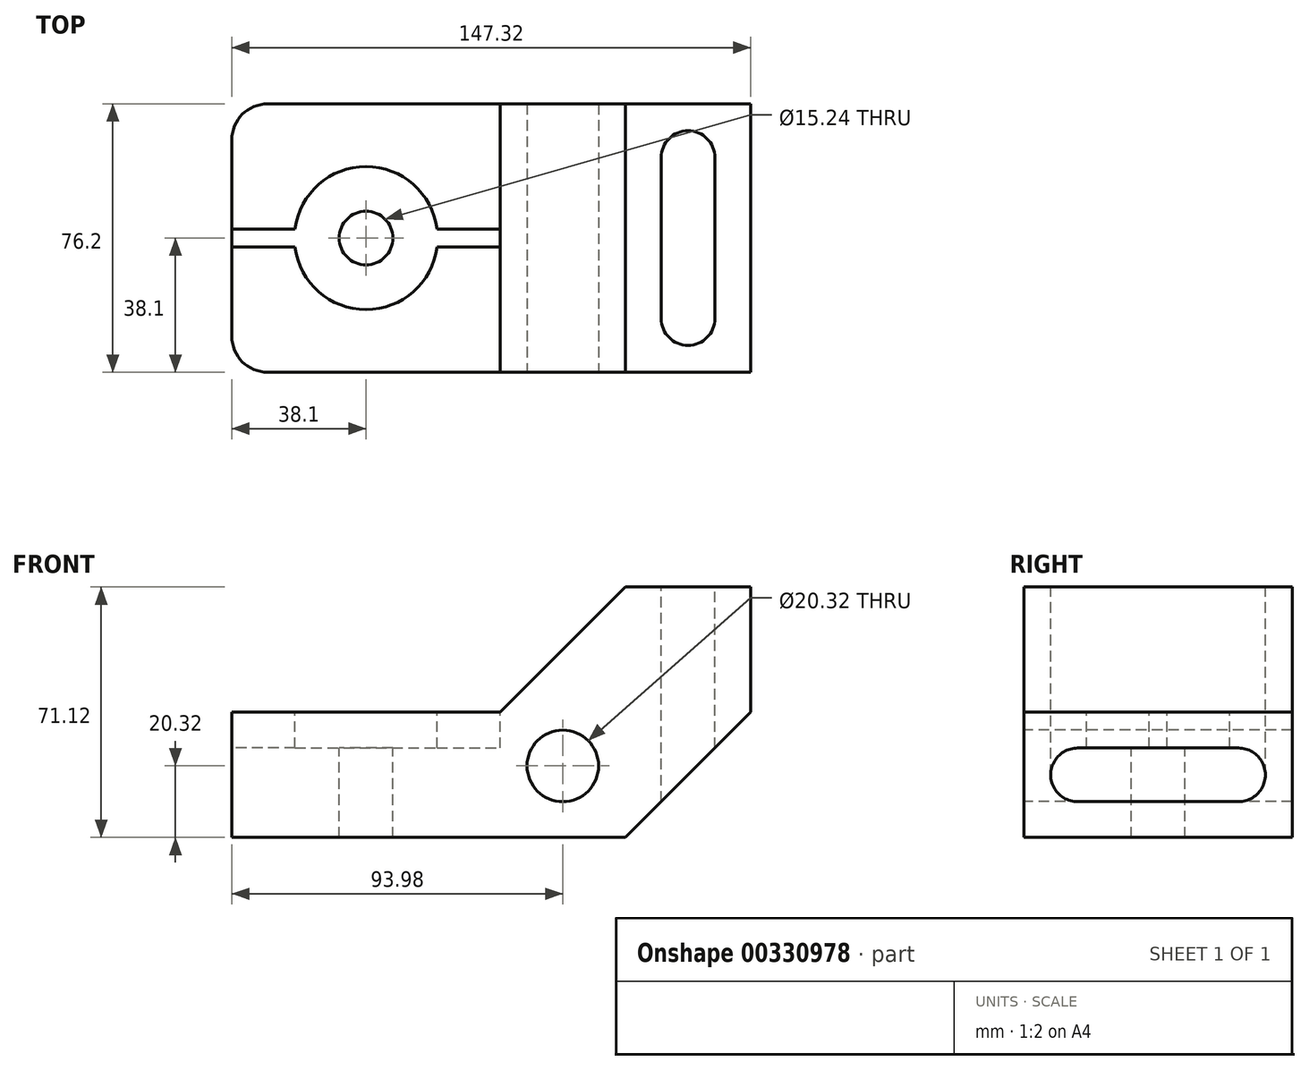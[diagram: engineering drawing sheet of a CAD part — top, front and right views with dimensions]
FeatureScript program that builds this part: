
annotation { "Feature Type Name" : "Feature", "Feature Type Description" : "" }
export const myFeature = defineFeature(function(context is Context, id is Id, definition is map)
    precondition{}
    {
        {
            var Q0;
            Q0=qCreatedBy(makeId("Front.planeOp"),FACE);
            var sketch = newSketch(context, id + "F0", { "sketchPlane" : qUnion([Q0])});
            skLineSegment(sketch, "E0.bottom", {"start": v(0, 0) * mm, "end": v(111.76, 0) * mm});
            skLineSegment(sketch, "E0.top", {"start": v(111.76, 71.12) * mm, "end": v(147.32, 71.12) * mm});
            skLineSegment(sketch, "E0.left", {"start": v(0, 0) * mm, "end": v(0, 35.56) * mm});
            skLineSegment(sketch, "E0.right", {"start": v(147.32, 35.56) * mm, "end": v(147.32, 71.12) * mm});
            skLineSegment(sketch, "E1", {"start": v(0, 35.56) * mm, "end": v(76.2, 35.56) * mm});
            skLineSegment(sketch, "E2", {"start": v(76.2, 35.56) * mm, "end": v(111.76, 71.12) * mm});
            skLineSegment(sketch, "E3", {"start": v(147.32, 71.12) * mm, "end": v(147.32, 35.56) * mm});
            skLineSegment(sketch, "E4", {"start": v(147.32, 35.56) * mm, "end": v(111.76, 0) * mm});
            skLineSegment(sketch, "E5", {"start": v(111.76, 0) * mm, "end": v(0, 0) * mm});
            skPoint(sketch, "E6.orphan", {"position": v(0, 71.12) * mm});
            skPoint(sketch, "E7.orphan", {"position": v(147.32, 0) * mm});
            skSolve(sketch);
        }
        {
            var Q0;
            Q0 = qSketchRegion(id + "F0", true);
            extrude(context, id + "F1", {"entities" : qUnion([Q0]), "depth" : 76.2 * mm});
        }
        {
            var Q0;
            Q0=makeQuery(id+"F1.opExtrude","CAP_FACE",FACE,{"disambiguationData":[OSD([sQuery(id+"F0.wireOp",EDGE,"E0.left"),sQuery(id+"F0.wireOp",EDGE,"E1"),sQuery(id+"F0.wireOp",EDGE,"E2"),sQuery(id+"F0.wireOp",EDGE,"E0.top"),sQuery(id+"F0.wireOp",EDGE,"E3"),sQuery(id+"F0.wireOp",EDGE,"E4"),sQuery(id+"F0.wireOp",EDGE,"E5")])],"isStart":false});
            var sketch = newSketch(context, id + "F2", { "sketchPlane" : qUnion([Q0])});
            skCircle(sketch, "E8", {"center": v(93.98, 20.32) * mm, "radius": 10.16 * mm});
            skSolve(sketch);
        }
        {
            var Q0;
            Q0 = qSketchRegion(id + "F2", true);
            extrude(context, id + "F3", {"entities" : qUnion([Q0]), "operationType" : NewBodyOperationType.REMOVE, "endBound" : BoundingType.THROUGH_ALL, "oppositeDirection" : true, "depth" : 25.4 * mm});
        }
        {
            var Q0;
            Q0=makeQuery(id+"F1.opExtrude","SWEPT_FACE",FACE,{"disambiguationData":[OSD([sQuery(id+"F0.wireOp",EDGE,"E1")])]});
            var sketch = newSketch(context, id + "F4", { "sketchPlane" : qUnion([Q0])});
            skCircle(sketch, "E9", {"center": v(38.1, -38.1) * mm, "radius": 7.62 * mm});
            skPoint(sketch, "E9.centerSnap0", {"position": v(0, -38.1) * mm});
            skPoint(sketch, "E9.centerSnap1", {"position": v(38.1, 0) * mm});
            skSolve(sketch);
        }
        {
            var Q0;
            Q0 = qSketchRegion(id + "F4", true);
            extrude(context, id + "F5", {"entities" : qUnion([Q0]), "operationType" : NewBodyOperationType.REMOVE, "endBound" : BoundingType.THROUGH_ALL, "oppositeDirection" : true, "depth" : 25.4 * mm});
        }
        {
            var Q0;
            Q0=makeQuery(id+"F1.opExtrude","SWEPT_FACE",FACE,{"disambiguationData":[OSD([sQuery(id+"F0.wireOp",EDGE,"E1")])]});
            var sketch = newSketch(context, id + "F6", { "sketchPlane" : qUnion([Q0])});
            skArc(sketch, "E10", {"start": v(17.94, -40.64) * mm, "mid": v(38.1, -58.42) * mm, "end": v(58.26, -40.64) * mm});
            skLineSegment(sketch, "E11", {"start": v(58.26, -35.56) * mm, "end": v(76.2, -35.56) * mm});
            skLineSegment(sketch, "E12", {"start": v(58.26, -40.64) * mm, "end": v(76.2, -40.64) * mm});
            skLineSegment(sketch, "E13", {"start": v(17.94, -40.64) * mm, "end": v(0, -40.64) * mm});
            skLineSegment(sketch, "E14", {"start": v(17.94, -35.56) * mm, "end": v(0, -35.56) * mm});
            skLineSegment(sketch, "E15", {"start": v(38.1, -38.1) * mm, "end": v(-36.03, -38.1) * mm, "construction": true});
            skLineSegment(sketch, "E16", {"start": v(76.2, -35.56) * mm, "end": v(76.2, -40.64) * mm});
            skLineSegment(sketch, "E17", {"start": v(0, -40.64) * mm, "end": v(0, -35.56) * mm});
            skArc(sketch, "E18.trimOffspring", {"start": v(58.26, -35.56) * mm, "mid": v(38.1, -17.78) * mm, "end": v(17.94, -35.56) * mm});
            skSolve(sketch);
        }
        {
            var Q0;
            Q0 = qSketchRegion(id + "F6", true);
            extrude(context, id + "F7", {"entities" : qUnion([Q0]), "operationType" : NewBodyOperationType.REMOVE, "oppositeDirection" : true, "depth" : 10.16 * mm});
        }
        {
            var Q0;
            Q0=makeQuery(id+"F1.opExtrude","SWEPT_FACE",FACE,{"disambiguationData":[OSD([sQuery(id+"F0.wireOp",EDGE,"E0.top")])]});
            var sketch = newSketch(context, id + "F8", { "sketchPlane" : qUnion([Q0])});
            skLineSegment(sketch, "E19", {"start": v(121.92, -15.24) * mm, "end": v(121.92, -60.96) * mm});
            skLineSegment(sketch, "E20", {"start": v(137.16, -15.24) * mm, "end": v(137.16, -60.96) * mm});
            skArc(sketch, "E21", {"start": v(137.16, -15.24) * mm, "mid": v(129.54, -7.62) * mm, "end": v(121.92, -15.24) * mm});
            skArc(sketch, "E22", {"start": v(121.92, -60.96) * mm, "mid": v(129.54, -68.58) * mm, "end": v(137.16, -60.96) * mm});
            skSolve(sketch);
        }
        {
            var Q0;
            Q0 = qSketchRegion(id + "F8", true);
            extrude(context, id + "F9", {"entities" : qUnion([Q0]), "operationType" : NewBodyOperationType.REMOVE, "endBound" : BoundingType.THROUGH_ALL, "oppositeDirection" : true, "depth" : 25.4 * mm});
        }
        {
            var Q0;
            Q0=makeQuery(id+"F1.opExtrude","CAP_EDGE",EDGE,{"disambiguationData":[OSD([sQuery(id+"F0.wireOp",EDGE,"E0.left")])],"isStart":false});
            var Q1;
            Q1=makeQuery(id+"F1.opExtrude","CAP_EDGE",EDGE,{"disambiguationData":[OSD([sQuery(id+"F0.wireOp",EDGE,"E0.left")])],"isStart":true});
            fillet(context, id + "F10", {"entities" : qUnion([Q0, Q1]), "radius" : 10.16 * mm, "tangentPropagation" : true, "allowEdgeOverflow" : false});
        }
    });
